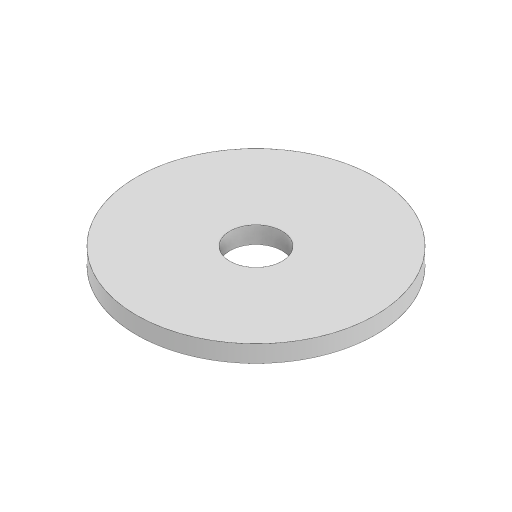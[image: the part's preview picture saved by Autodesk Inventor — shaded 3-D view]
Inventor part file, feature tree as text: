
AUTODESK INVENTOR PART (.ipt)
format: ipt  version: 2024 (Build 280153000, 153)  size: 87,040 bytes
history: native  units: mm
features: extrude x1, sketch x1
ambient origin geometry x8: Origin, YZ Plane, XZ Plane, XY Plane, X Axis, Y Axis, Z Axis, Center Point
bodies: Solid1 (feature_tree)
feature tree (2):
  extrude  "Extrusion1"  Depth=4.0mm
  sketch  "Sketch1"  dims[d0=56.0mm d1=12.25mm d2=4.0mm d3=0.0mm]
